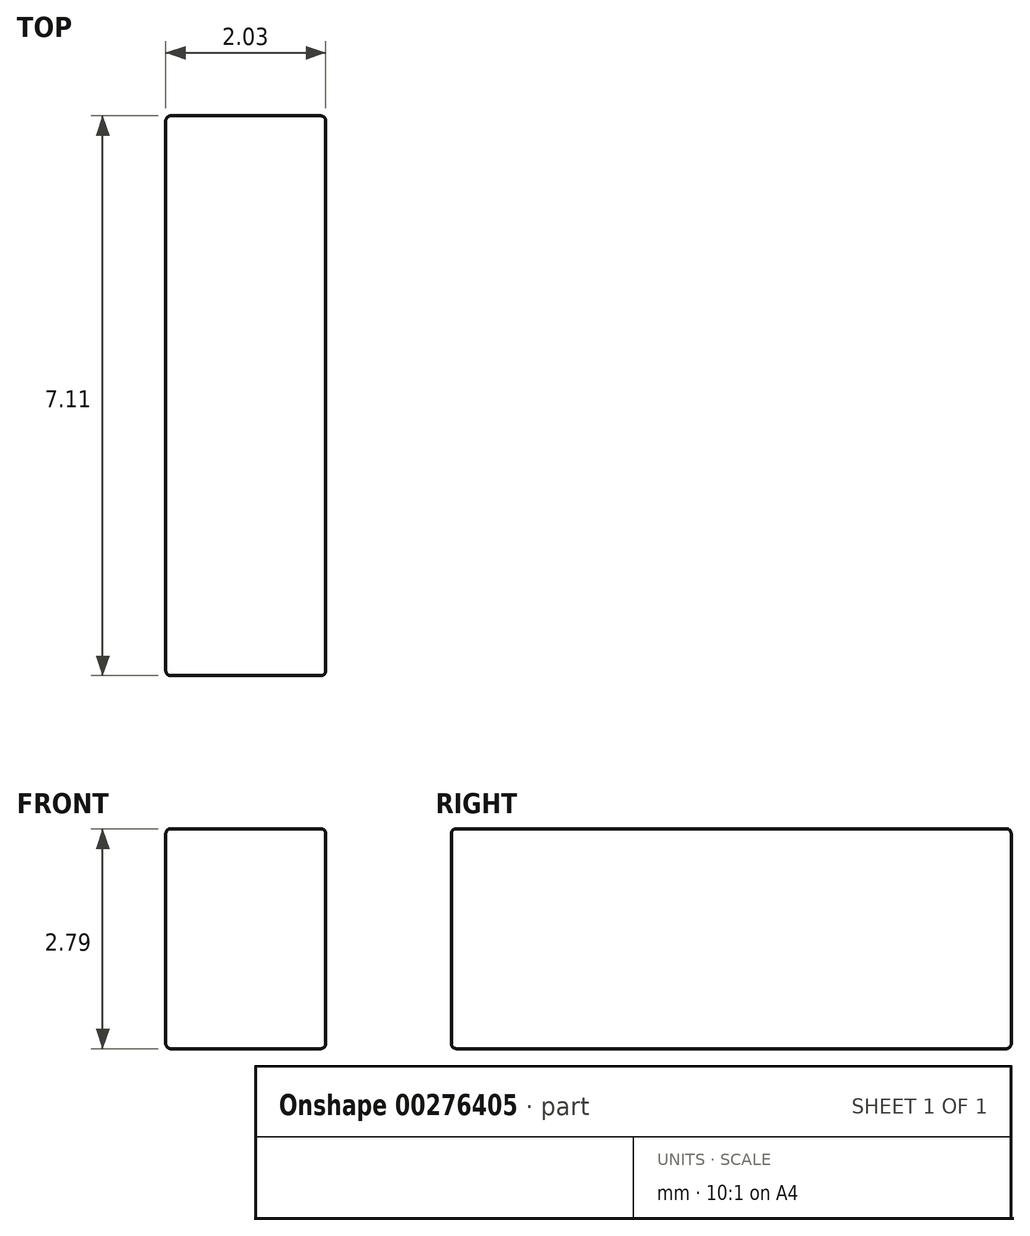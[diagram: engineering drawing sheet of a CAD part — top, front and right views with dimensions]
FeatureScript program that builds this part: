
annotation { "Feature Type Name" : "Feature", "Feature Type Description" : "" }
export const myFeature = defineFeature(function(context is Context, id is Id, definition is map)
    precondition{}
    {
        {
            var Q0;
            Q0=qCreatedBy(makeId("Front.planeOp"),FACE);
            var sketch = newSketch(context, id + "F0", { "sketchPlane" : qUnion([Q0])});
            skLineSegment(sketch, "E0.bottom", {"start": v(0, 0) * mm, "end": v(2.03, 0) * mm});
            skLineSegment(sketch, "E0.top", {"start": v(0, 2.8) * mm, "end": v(2.03, 2.8) * mm});
            skLineSegment(sketch, "E0.left", {"start": v(0, 0) * mm, "end": v(0, 2.8) * mm});
            skLineSegment(sketch, "E0.right", {"start": v(2.03, 0) * mm, "end": v(2.03, 2.8) * mm});
            skSolve(sketch);
        }
        {
            var Q0;
            Q0 = qSketchRegion(id + "F0", true);
            extrude(context, id + "F1", {"entities" : qUnion([Q0]), "depth" : 7.11 * mm, "offsetDistance" : 25.4 * mm});
        }
        {
            var Q0;
            Q0=makeQuery(id+"F1.opExtrude","CAP_FACE",FACE,{"disambiguationData":[OSD([sQuery(id+"F0.wireOp",EDGE,"E0.bottom"),sQuery(id+"F0.wireOp",EDGE,"E0.top"),sQuery(id+"F0.wireOp",EDGE,"E0.left"),sQuery(id+"F0.wireOp",EDGE,"E0.right")])],"isStart":false});
            var Q1;
            Q1=makeQuery(id+"F1.opExtrude","SWEPT_FACE",FACE,{"disambiguationData":[OSD([sQuery(id+"F0.wireOp",EDGE,"E0.right")])]});
            var Q2;
            Q2=makeQuery(id+"F1.opExtrude","SWEPT_FACE",FACE,{"disambiguationData":[OSD([sQuery(id+"F0.wireOp",EDGE,"E0.top")])]});
            var Q3;
            Q3=makeQuery(id+"F1.opExtrude","SWEPT_FACE",FACE,{"disambiguationData":[OSD([sQuery(id+"F0.wireOp",EDGE,"E0.left")])]});
            var Q4;
            Q4=makeQuery(id+"F1.opExtrude","SWEPT_FACE",FACE,{"disambiguationData":[OSD([sQuery(id+"F0.wireOp",EDGE,"E0.bottom")])]});
            var Q5;
            Q5=makeQuery(id+"F1.opExtrude","CAP_FACE",FACE,{"disambiguationData":[OSD([sQuery(id+"F0.wireOp",EDGE,"E0.bottom"),sQuery(id+"F0.wireOp",EDGE,"E0.top"),sQuery(id+"F0.wireOp",EDGE,"E0.left"),sQuery(id+"F0.wireOp",EDGE,"E0.right")])],"isStart":true});
            fillet(context, id + "F2", {"entities" : qUnion([Q0, Q1, Q2, Q3, Q4, Q5]), "tangentPropagation" : true, "radius" : 0.06 * mm, "defaultsChanged" : true, "vertexSettings" : [], "allowEdgeOverflow" : false});
        }
    });
